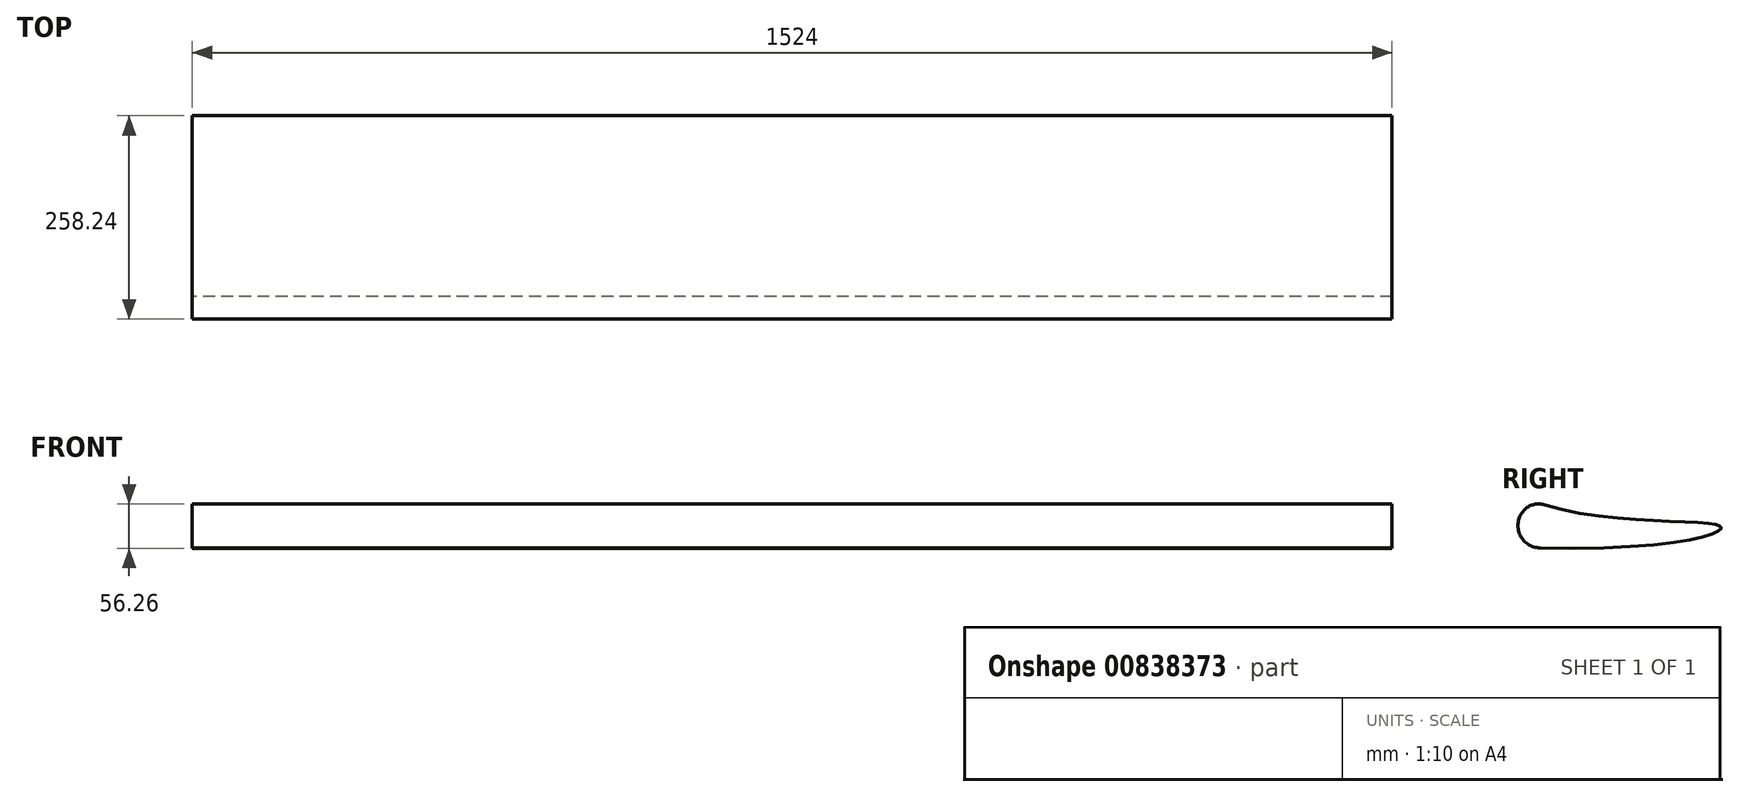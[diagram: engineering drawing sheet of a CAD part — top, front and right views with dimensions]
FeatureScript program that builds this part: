
annotation { "Feature Type Name" : "Feature", "Feature Type Description" : "" }
export const myFeature = defineFeature(function(context is Context, id is Id, definition is map)
    precondition{}
    {
        {
            var Q0;
            Q0=qCreatedBy(makeId("Right.planeOp"),FACE);
            var sketch = newSketch(context, id + "F0", { "sketchPlane" : qUnion([Q0])});
            skPoint(sketch, "E0.middle", {"position": v(203.08, 0) * mm});
            skFitSpline(sketch, "E1", {"points": [v(-20.16, 28.23) * mm, v(205.61, 0.57) * mm, v(-20.16, -28.23) * mm], "startDerivative": vector(475.5, -168.19) * mm, "endDerivative": vector(-1042.72, 27.68) * mm});
            skPoint(sketch, "E2.orphan", {"position": v(205.61, 25.97) * mm});
            skPoint(sketch, "E3.trimOffspring.end.orphan", {"position": v(205.61, -24.83) * mm});
            skArc(sketch, "E4.trimOffspring", {"start": v(-39.4, 20.66) * mm, "mid": v(-46.43, -10.34) * mm, "end": v(-20.16, -28.23) * mm});
            skArc(sketch, "E5.filletArc", {"start": v(-14.27, 26.24) * mm, "mid": v(-27.6, 26.87) * mm, "end": v(-39.4, 20.66) * mm});
            skSolve(sketch);
        }
        {
            var Q0;
            Q0=makeQuery(id+"F0.imprint","IMPRINT",FACE,{"disambiguationData":[TD([[makeQuery(id+"F0.imprint","IMPRINT",EDGE,{"derivedFrom":sQuery(id+"F0.wireOp",EDGE,"E1")}),-1.0]])]});
            extrude(context, id + "F1", {"entities" : qUnion([Q0]), "depth" : 1524 * mm, "offsetDistance" : 25.4 * mm});
        }
    });
